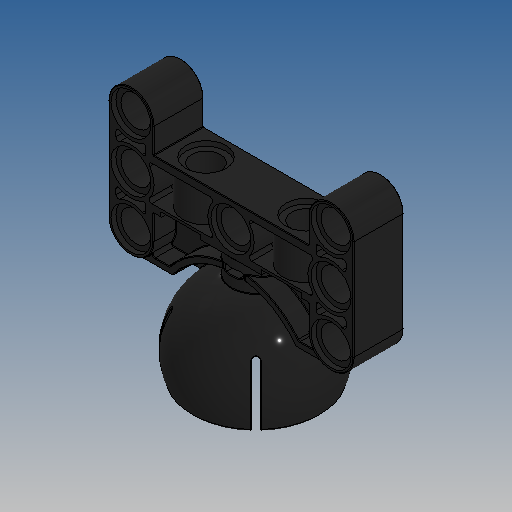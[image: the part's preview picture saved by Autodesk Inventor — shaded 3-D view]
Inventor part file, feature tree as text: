
AUTODESK INVENTOR PART (.ipt)
format: ipt  version: 2025 (Build 290162010, 162A)  size: 1,420,288 bytes
history: native  units: mm
features: sketch x11, extrude x9, fillet x5, projected_geometry x4, mirror x2, hole x1, revolve x1, delete_face x1, plane x1, pattern_circular x1
ambient origin geometry x8: Origin, YZ Plane, XZ Plane, XY Plane, X Axis, Y Axis, Z Axis, Center Point
bodies: Volumenkörper1 (feature_tree)
feature tree (36):
  extrude  "Extrusion1"  Depth=16.0mm
  extrude  "Extrusion2"  Depth=8.0mm
  extrude  "Extrusion3"  Depth=8.0mm
  extrude  "Extrusion4"  Depth=6.4mm
  hole  "Bohrung1"  [1 undecoded]
  fillet  "Rundung1"  Radius=1.2mm
  mirror  "Spiegeln1"
  extrude  "Extrusion5"  Depth=1.2mm
  revolve  "Umdrehung1"
  fillet  "Rundung2"  Radius=0.4mm
  extrude  "Extrusion7"  Depth=3.6mm TaperAngle=0.0deg
  extrude  "Extrusion8"  Depth=7.4mm
  delete_face  "Fläche löschen1"
  extrude  "Extrusion6"  Depth=0.1mm
  fillet  "Rundung3"  Radius=0.8mm
  fillet  "Rundung4"  Radius=19.0mm
  plane  "Arbeitsebene1"
  mirror  "Spiegeln2"
  extrude  "Extrusion9"  Depth=0.1mm
  fillet  "Rundung5"  Radius=11.0mm
  pattern_circular  "Runde Anordnung1"  [2 undecoded]
  sketch  "Skizze1"  dims[d0=4.8mm d1=16.0mm]
  sketch  "Skizze2"  dims[d2=8.0mm d3=8.0mm]
  sketch  "Skizze3"  dims[d4=7.2mm d5=8.0mm]
  sketch  "Skizze4"  dims[d6=4.0mm d7=0.0mm d8=6.4mm]
  sketch  "Skizze5"  dims[d9=0.8mm d10=0.0mm d11=3.7mm d12=1.2mm]
  sketch  "Skizze6"  dims[d13=1.2mm d14=1.2mm d15=0.4mm]
  sketch  "Skizze7"  dims[d17=1.2mm d18=3.6mm d19=0.0mm]
  sketch  "Skizze8"  dims[d20=8.0mm d21=7.4mm]
  sketch  "Skizze9"  dims[d22=3.6mm d23=0.0mm]
  projected_geometry  "Projizierte Kontur1"
  projected_geometry  "Projizierte Kontur2"
  projected_geometry  "Projizierte Kontur3"
  projected_geometry  "Projizierte Kontur4"
  sketch  "Skizze10"  dims[d24=4.6mm d25=6.0mm d26=6.4mm d27=0.8mm d28=90.0deg d29=8.0mm d30=20.594885mm d31=0.1mm d32=0.8mm d33=0.0mm d34=19.0mm]
  sketch  "Skizze11"  dims[d35=28.0mm d36=23.0mm d37=11.0mm d38=3.9mm d40=8.789392mm d41=180.0deg d42=1.0mm d43=1.5mm d44=3.0mm d45=0.0mm d46=0.0mm d47=2.0mm d48=0.5mm d49=10.0mm d50=3.0mm d51=0.5mm d52=0.8mm d53=0.0mm d54=0.4mm d55=1.0mm d56=1.0mm d57=1.5mm d58=0.0mm d59=7.0mm d60=0.0mm d61=0.1mm d62=45.0deg d63=1.0mm d64=17.0mm d65=0.0mm d66=0.0mm d67=20.0mm d68=90.0deg d70=0.1mm]
note: 3 required parameter values undecoded (feature->parameter linkage not recoverable at this tier; creation-order binding heuristic only, values carry confidence <= 0.55)
